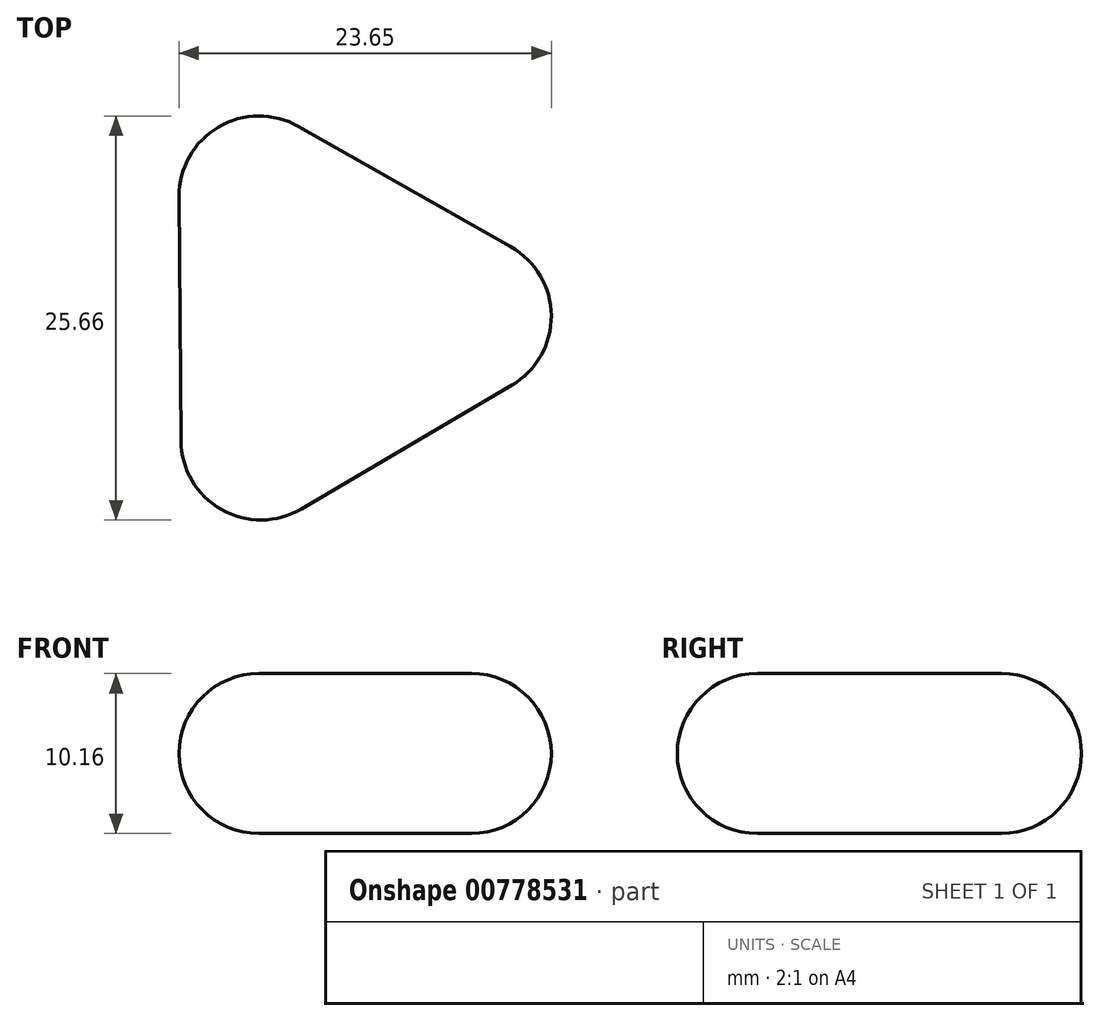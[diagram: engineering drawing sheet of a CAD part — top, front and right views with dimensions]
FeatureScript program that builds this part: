
annotation { "Feature Type Name" : "Feature", "Feature Type Description" : "" }
export const myFeature = defineFeature(function(context is Context, id is Id, definition is map)
    precondition{}
    {
        {
            var Q0;
            Q0=qCreatedBy(makeId("Top.planeOp"),FACE);
            var sketch = newSketch(context, id + "F0", { "sketchPlane" : qUnion([Q0])});
            skCircle(sketch, "E0.cCircle", {"center": v(0, 0) * mm, "radius": 9.55 * mm, "construction": true});
            skLineSegment(sketch, "E0.0", {"start": v(-9.69, 16.47) * mm, "end": v(19.1, 0.15) * mm});
            skLineSegment(sketch, "E0.1", {"start": v(19.1, 0.15) * mm, "end": v(-9.42, -16.63) * mm});
            skLineSegment(sketch, "E0.2", {"start": v(-9.42, -16.63) * mm, "end": v(-9.69, 16.47) * mm});
            skPoint(sketch, "E0.0.midPoint", {"position": v(4.71, 8.31) * mm});
            skSolve(sketch);
        }
        {
            var Q0;
            Q0=makeQuery(id+"F0.imprint","IMPRINT",FACE,{"disambiguationData":[TD([[makeQuery(id+"F0.imprint","IMPRINT",EDGE,{"derivedFrom":sQuery(id+"F0.wireOp",EDGE,"E0.0")}),-1.0]])]});
            extrude(context, id + "F1", {"entities" : qUnion([Q0]), "depth" : 10.16 * mm, "offsetDistance" : 25.4 * mm});
        }
        {
            var Q0;
            Q0=makeQuery(id+"F1.opExtrude","SWEPT_EDGE",EDGE,{"disambiguationData":[OSD([sQuery(id+"F0.wireOp",EDGE,"E0.1"),sQuery(id+"F0.wireOp",EDGE,"E0.2")])]});
            var Q1;
            Q1=makeQuery(id+"F1.opExtrude","SWEPT_EDGE",EDGE,{"disambiguationData":[OSD([sQuery(id+"F0.wireOp",EDGE,"E0.0"),sQuery(id+"F0.wireOp",EDGE,"E0.1")])]});
            var Q2;
            Q2=makeQuery(id+"F1.opExtrude","SWEPT_EDGE",EDGE,{"disambiguationData":[OSD([sQuery(id+"F0.wireOp",EDGE,"E0.0"),sQuery(id+"F0.wireOp",EDGE,"E0.2")])]});
            fillet(context, id + "F2", {"entities" : qUnion([Q0, Q1, Q2]), "radius" : 5.08 * mm, "tangentPropagation" : true, "allowEdgeOverflow" : false});
        }
        {
            var Q0;
            Q0=makeQuery(id+"F1.opExtrude","CAP_FACE",FACE,{"disambiguationData":[OSD([sQuery(id+"F0.wireOp",EDGE,"E0.0"),sQuery(id+"F0.wireOp",EDGE,"E0.1"),sQuery(id+"F0.wireOp",EDGE,"E0.2")])],"isStart":true});
            var Q1;
            Q1=makeQuery(id+"F1.opExtrude","CAP_FACE",FACE,{"disambiguationData":[OSD([sQuery(id+"F0.wireOp",EDGE,"E0.0"),sQuery(id+"F0.wireOp",EDGE,"E0.1"),sQuery(id+"F0.wireOp",EDGE,"E0.2")])],"isStart":false});
            fillet(context, id + "F3", {"entities" : qUnion([Q0, Q1]), "radius" : 5.08 * mm, "tangentPropagation" : true, "allowEdgeOverflow" : false});
        }
    });
